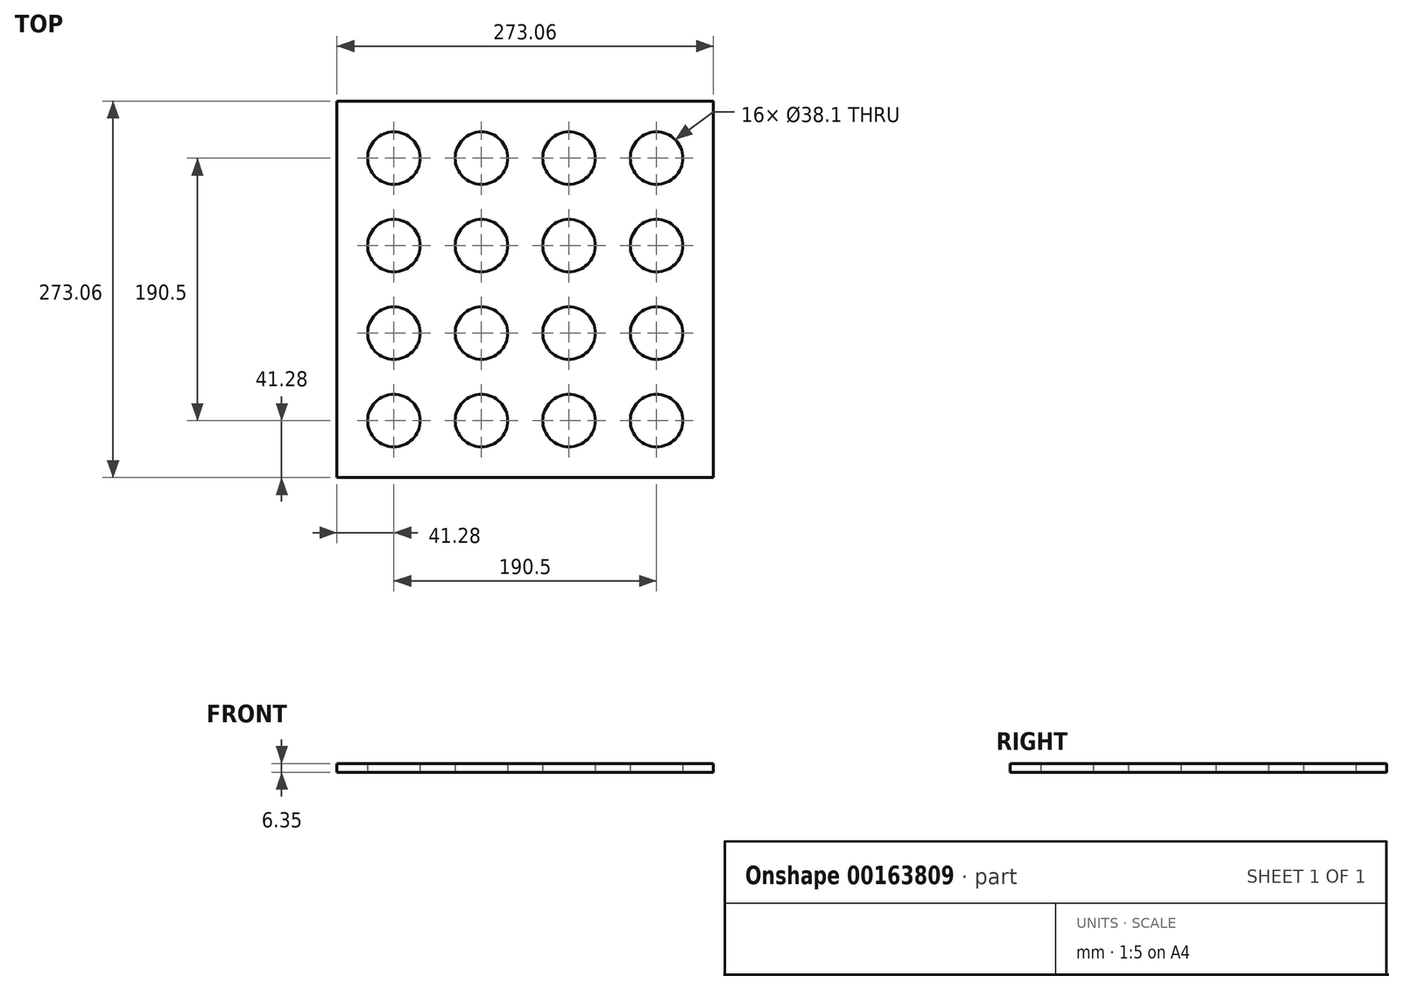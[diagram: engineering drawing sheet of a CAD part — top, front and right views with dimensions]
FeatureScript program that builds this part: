
annotation { "Feature Type Name" : "Feature", "Feature Type Description" : "" }
export const myFeature = defineFeature(function(context is Context, id is Id, definition is map)
    precondition{}
    {
        {
            var Q0;
            Q0=qCreatedBy(makeId("Top.planeOp"),FACE);
            var sketch = newSketch(context, id + "F0", { "sketchPlane" : qUnion([Q0])});
            skLineSegment(sketch, "E0.bottom", {"start": v(136.53, 136.53) * mm, "end": v(-136.53, 136.53) * mm});
            skLineSegment(sketch, "E0.top", {"start": v(136.53, -136.53) * mm, "end": v(-136.53, -136.53) * mm});
            skLineSegment(sketch, "E0.left", {"start": v(136.53, 136.53) * mm, "end": v(136.53, -136.53) * mm});
            skLineSegment(sketch, "E0.right", {"start": v(-136.53, 136.53) * mm, "end": v(-136.53, -136.53) * mm});
            skPoint(sketch, "E0.middle", {"position": v(0, 0) * mm});
            skLineSegment(sketch, "E1.top", {"start": v(-136.53, -95.25) * mm, "end": v(-95.25, -95.25) * mm, "construction": true});
            skLineSegment(sketch, "E1.right", {"start": v(-95.25, -136.53) * mm, "end": v(-95.25, -95.25) * mm, "construction": true});
            skCircle(sketch, "E2", {"center": v(-95.25, -95.25) * mm, "radius": 19.05 * mm});
            skCircle(sketch, "E3.0.1.0", {"center": v(-95.25, -31.75) * mm, "radius": 19.05 * mm});
            skCircle(sketch, "E3.0.2.0", {"center": v(-95.25, 31.75) * mm, "radius": 19.05 * mm});
            skCircle(sketch, "E3.0.3.0", {"center": v(-95.25, 95.25) * mm, "radius": 19.05 * mm});
            skCircle(sketch, "E3.1.0.0", {"center": v(-31.75, -95.25) * mm, "radius": 19.05 * mm});
            skCircle(sketch, "E3.1.1.0", {"center": v(-31.75, -31.75) * mm, "radius": 19.05 * mm});
            skCircle(sketch, "E3.1.2.0", {"center": v(-31.75, 31.75) * mm, "radius": 19.05 * mm});
            skCircle(sketch, "E3.1.3.0", {"center": v(-31.75, 95.25) * mm, "radius": 19.05 * mm});
            skCircle(sketch, "E3.2.0.0", {"center": v(31.75, -95.25) * mm, "radius": 19.05 * mm});
            skCircle(sketch, "E3.2.1.0", {"center": v(31.75, -31.75) * mm, "radius": 19.05 * mm});
            skCircle(sketch, "E3.2.2.0", {"center": v(31.75, 31.75) * mm, "radius": 19.05 * mm});
            skCircle(sketch, "E3.2.3.0", {"center": v(31.75, 95.25) * mm, "radius": 19.05 * mm});
            skCircle(sketch, "E3.3.0.0", {"center": v(95.25, -95.25) * mm, "radius": 19.05 * mm});
            skCircle(sketch, "E3.3.1.0", {"center": v(95.25, -31.75) * mm, "radius": 19.05 * mm});
            skCircle(sketch, "E3.3.2.0", {"center": v(95.25, 31.75) * mm, "radius": 19.05 * mm});
            skCircle(sketch, "E3.3.3.0", {"center": v(95.25, 95.25) * mm, "radius": 19.05 * mm});
            skLineSegment(sketch, "E3.direction1", {"start": v(-95.25, -95.25) * mm, "end": v(-31.75, -95.25) * mm, "construction": true});
            skLineSegment(sketch, "E3.direction2", {"start": v(-95.25, -95.25) * mm, "end": v(-95.25, -31.75) * mm, "construction": true});
            skSolve(sketch);
        }
        {
            var Q0;
            Q0=makeQuery(id+"F0.imprint","IMPRINT",FACE,{"disambiguationData":[TD([[makeQuery(id+"F0.imprint","IMPRINT",EDGE,{"derivedFrom":sQuery(id+"F0.wireOp",EDGE,"E0.bottom")}),1.0]])]});
            extrude(context, id + "F1", {"entities" : qUnion([Q0]), "depth" : 6.35 * mm});
        }
    });
